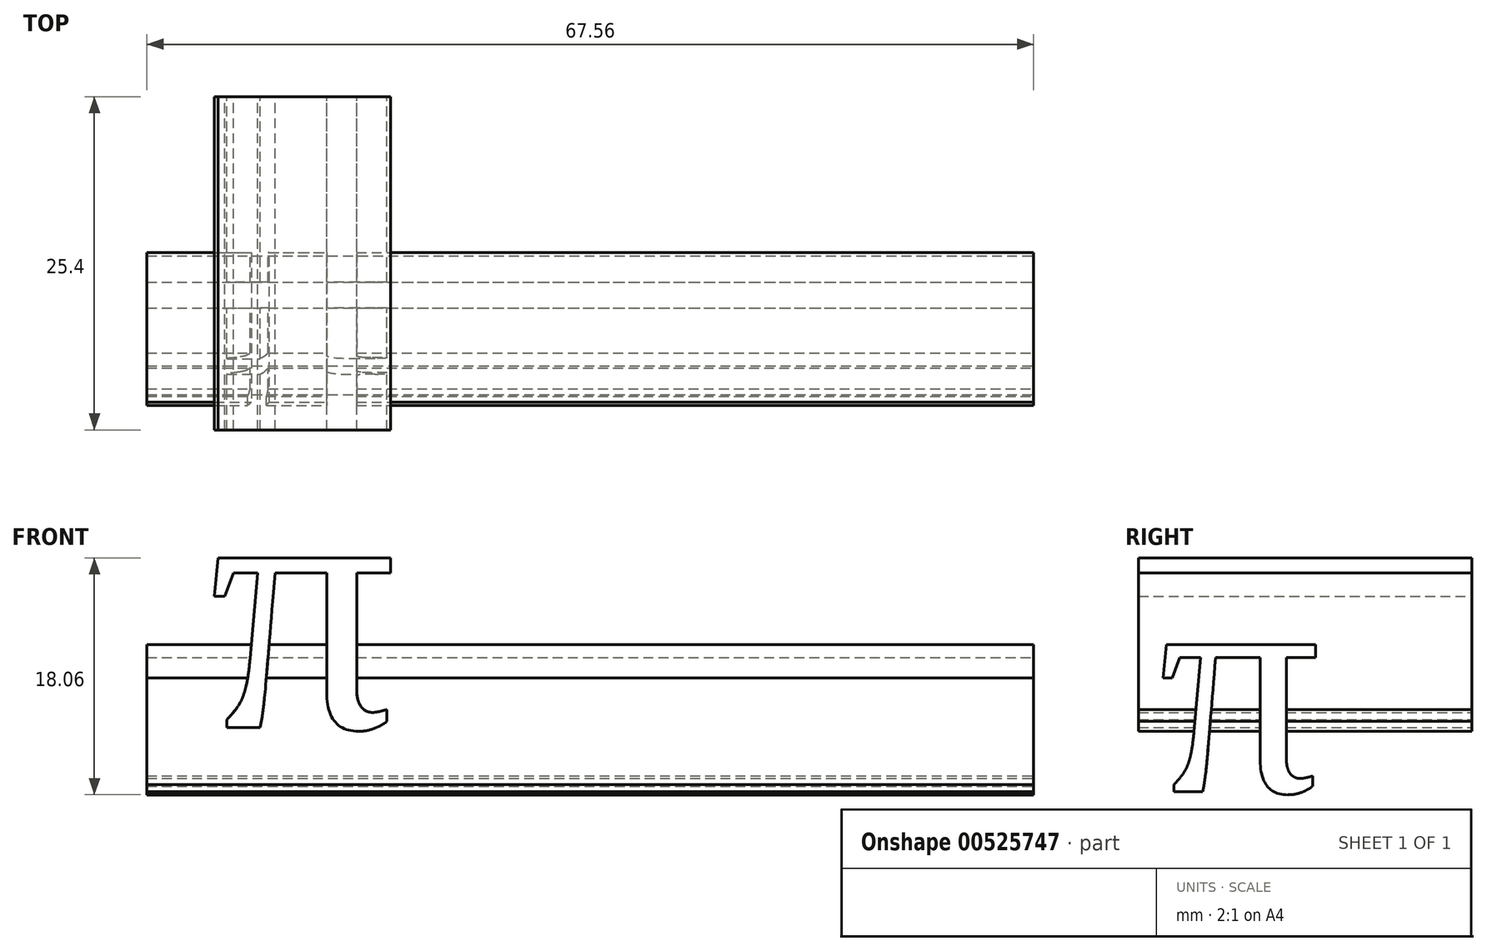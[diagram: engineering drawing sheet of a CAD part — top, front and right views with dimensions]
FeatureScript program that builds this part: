
annotation { "Feature Type Name" : "Feature", "Feature Type Description" : "" }
export const myFeature = defineFeature(function(context is Context, id is Id, definition is map)
    precondition{}
    {
        {
            var Q0;
            Q0=qCreatedBy(makeId("Front.planeOp"),FACE);
            var sketch = newSketch(context, id + "F0", { "sketchPlane" : qUnion([Q0])});
            skText(sketch, "E0", { "text": "π", "fontName": "Tinos-Regular.ttf"});
            const initialGuessF0  = {"E0": [-0.0628, 0.0284, 1, 0, 0.0203]};
            skSetInitialGuess(sketch, initialGuessF0);
            skSolve(sketch);
        }
        {
            var Q0;
            Q0 = qSketchRegion(id + "F0", true);
            extrude(context, id + "F1", {"entities" : qUnion([Q0]), "depth" : 25.4 * mm, "offsetDistance" : 25.4 * mm});
        }
        {
            var Q0;
            Q0=qCreatedBy(makeId("Right.planeOp"),FACE);
            var sketch = newSketch(context, id + "F2", { "sketchPlane" : qUnion([Q0])});
            skText(sketch, "E1", { "text": "π", "fontName": "Tinos-Regular.ttf"});
            const initialGuessF2  = {"E1": [-0.02386, 0.02352, 1, 0, 0.01758]};
            skSetInitialGuess(sketch, initialGuessF2);
            skSolve(sketch);
        }
        {
            var Q0;
            Q0 = qSketchRegion(id + "F2", true);
            extrude(context, id + "F3", {"entities" : qUnion([Q0]), "operationType" : NewBodyOperationType.ADD, "oppositeDirection" : true, "depth" : 67.56 * mm, "offsetDistance" : 25.4 * mm});
        }
    });
